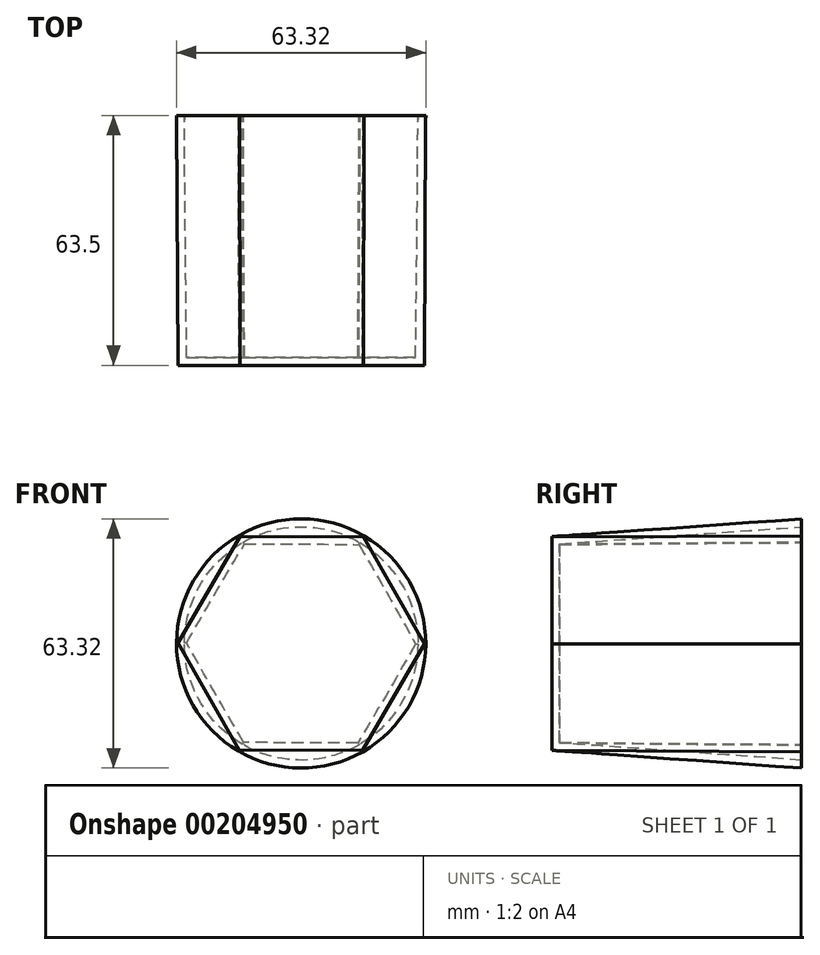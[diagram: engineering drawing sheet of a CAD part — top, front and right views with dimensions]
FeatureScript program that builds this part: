
annotation { "Feature Type Name" : "Feature", "Feature Type Description" : "" }
export const myFeature = defineFeature(function(context is Context, id is Id, definition is map)
    precondition{}
    {
        {
            var Q0;
            Q0=qCreatedBy(makeId("Front.planeOp"),FACE);
            var sketch = newSketch(context, id + "F0", { "sketchPlane" : qUnion([Q0])});
            skCircle(sketch, "E0", {"center": v(0, 0) * mm, "radius": 31.66 * mm});
            skSolve(sketch);
        }
        {
            var Q0;
            Q0=makeQuery(id+"F0.imprint","IMPRINT",FACE,{"disambiguationData":[TD([[makeQuery(id+"F0.imprint","IMPRINT",EDGE,{"derivedFrom":sQuery(id+"F0.wireOp",EDGE,"E0")}),1.0]])]});
            cPlane(context, id + "F1", {"entities" : qUnion([Q0]), "cplaneType" : CPlaneType.OFFSET, "offset" : 63.5 * mm, "width" : 152.4 * mm, "height" : 152.4 * mm});
        }
        {
            var Q0;
            Q0=qCreatedBy(id+"F1.planeOp",FACE);
            var sketch = newSketch(context, id + "F2", { "sketchPlane" : qUnion([Q0])});
            skCircle(sketch, "E1.cCircle", {"center": v(0, 0) * mm, "radius": 27.13 * mm, "construction": true});
            skLineSegment(sketch, "E1.0", {"start": v(15.8, 27.05) * mm, "end": v(31.33, -0.15) * mm});
            skLineSegment(sketch, "E1.1", {"start": v(31.33, -0.15) * mm, "end": v(15.53, -27.2) * mm});
            skLineSegment(sketch, "E1.2", {"start": v(15.53, -27.2) * mm, "end": v(-15.8, -27.05) * mm});
            skLineSegment(sketch, "E1.3", {"start": v(-15.8, -27.05) * mm, "end": v(-31.33, 0.15) * mm});
            skLineSegment(sketch, "E1.4", {"start": v(-31.33, 0.15) * mm, "end": v(-15.53, 27.2) * mm});
            skLineSegment(sketch, "E1.5", {"start": v(-15.53, 27.2) * mm, "end": v(15.8, 27.05) * mm});
            skPoint(sketch, "E1.0.midPoint", {"position": v(23.56, 13.45) * mm});
            skSolve(sketch);
        }
        {
            var Q0;
            Q0=makeQuery(id+"F2.imprint","IMPRINT",FACE,{"disambiguationData":[TD([[makeQuery(id+"F2.imprint","IMPRINT",EDGE,{"derivedFrom":sQuery(id+"F2.wireOp",EDGE,"E1.0")}),-1.0]])]});
            var Q1;
            Q1=makeQuery(id+"F0.imprint","IMPRINT",FACE,{"disambiguationData":[TD([[makeQuery(id+"F0.imprint","IMPRINT",EDGE,{"derivedFrom":sQuery(id+"F0.wireOp",EDGE,"E0")}),1.0]])]});
            loft(context, id + "F3", {"sheetProfilesArray" : [{ "sheetProfileEntities" : qUnion([Q0]) }, { "sheetProfileEntities" : qUnion([Q1]) }]});
        }
        {
            var Q0;
            Q0=makeQuery(id+"F3.opLoft","CAP_FACE",FACE,{"disambiguationData":[OSD([makeQuery(id+"F0.imprint","IMPRINT",FACE,{"disambiguationData":[TD([[makeQuery(id+"F0.imprint","IMPRINT",EDGE,{"derivedFrom":sQuery(id+"F0.wireOp",EDGE,"E0")}),1.0]])]})])],"isStart":true});
            shell(context, id + "F4", {"entities" : qUnion([Q0]), "thickness" : 2 * mm});
        }
    });
